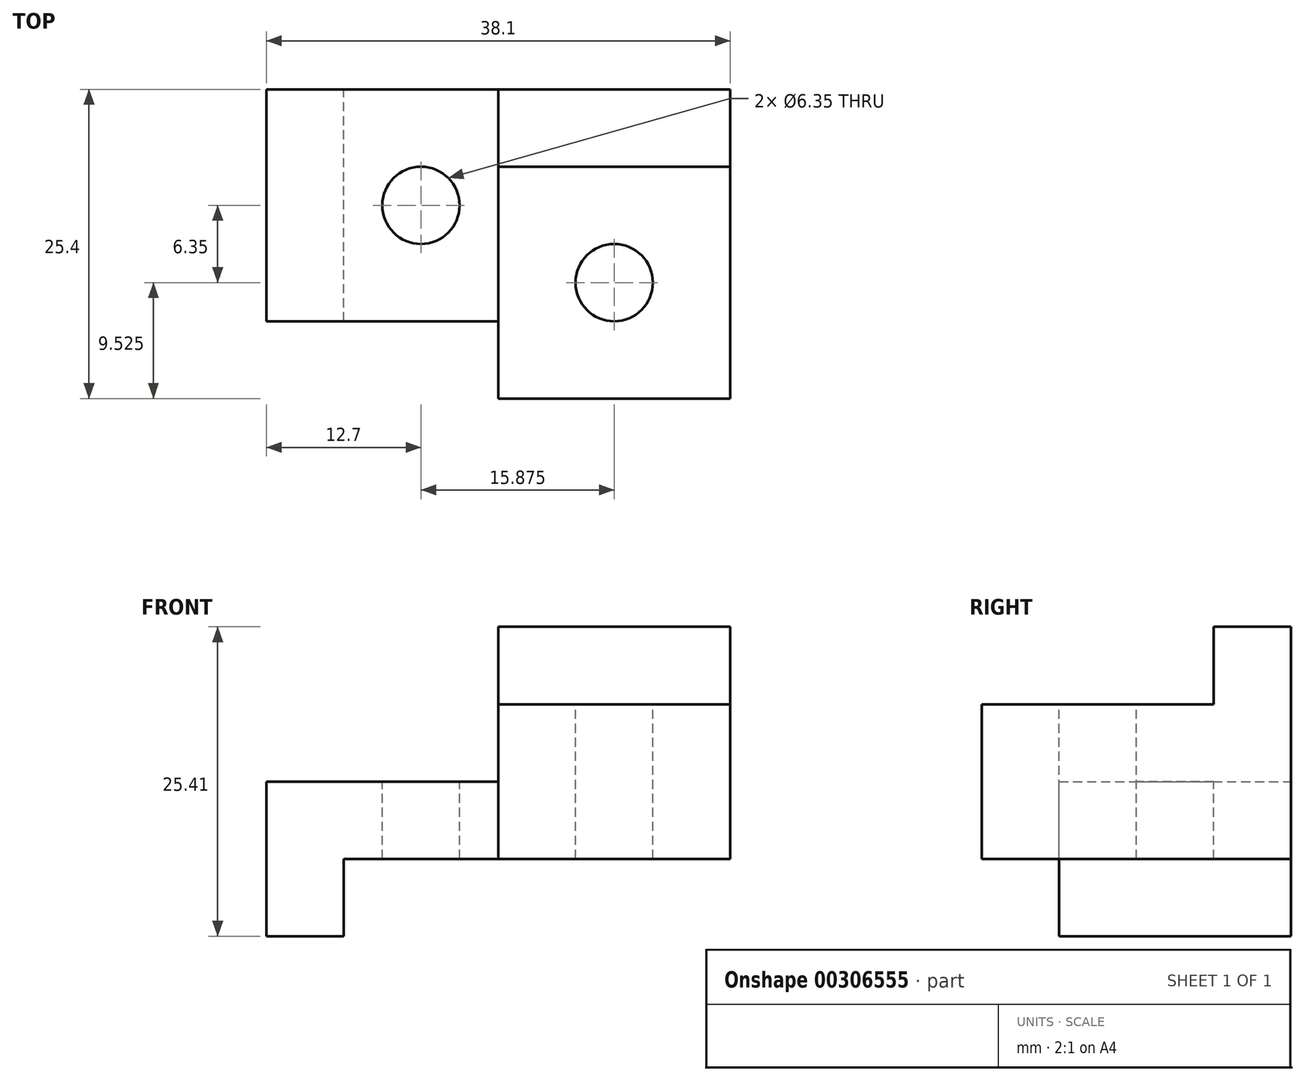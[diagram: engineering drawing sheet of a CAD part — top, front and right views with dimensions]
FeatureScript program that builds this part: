
annotation { "Feature Type Name" : "Feature", "Feature Type Description" : "" }
export const myFeature = defineFeature(function(context is Context, id is Id, definition is map)
    precondition{}
    {
        {
            var Q0;
            Q0=qCreatedBy(makeId("Front.planeOp"),FACE);
            var sketch = newSketch(context, id + "F0", { "sketchPlane" : qUnion([Q0])});
            skLineSegment(sketch, "E0", {"start": v(0, 0) * mm, "end": v(0, 12.7) * mm});
            skLineSegment(sketch, "E1", {"start": v(0, 12.7) * mm, "end": v(19.05, 12.7) * mm});
            skLineSegment(sketch, "E2", {"start": v(19.05, 6.35) * mm, "end": v(6.35, 6.35) * mm});
            skLineSegment(sketch, "E3", {"start": v(6.35, 6.35) * mm, "end": v(6.35, 0) * mm});
            skLineSegment(sketch, "E4", {"start": v(6.35, 0) * mm, "end": v(0, 0) * mm});
            skLineSegment(sketch, "E5", {"start": v(38.1, 25.4) * mm, "end": v(38.1, 6.35) * mm});
            skLineSegment(sketch, "E6", {"start": v(38.1, 6.35) * mm, "end": v(19.05, 6.35) * mm});
            skLineSegment(sketch, "E7", {"start": v(19.05, 6.35) * mm, "end": v(19.05, 12.7) * mm});
            skLineSegment(sketch, "E8", {"start": v(19.05, 12.7) * mm, "end": v(19.05, 25.4) * mm});
            skLineSegment(sketch, "E9", {"start": v(19.05, 25.4) * mm, "end": v(38.1, 25.4) * mm});
            skLineSegment(sketch, "E10", {"start": v(19.05, 19.05) * mm, "end": v(38.1, 19.05) * mm});
            skSolve(sketch);
        }
        {
            var Q0;
            Q0=makeQuery(id+"F0.imprint","IMPRINT",FACE,{"disambiguationData":[TD([[makeQuery(id+"F0.imprint","IMPRINT",EDGE,{"derivedFrom":sQuery(id+"F0.wireOp",EDGE,"E0")}),-1.0]])]});
            extrude(context, id + "F1", {"entities" : qUnion([Q0]), "depth" : 19.05 * mm});
        }
        {
            var Q0;
            {var subQ3=sQuery(id+"F0.wireOp",EDGE,"E6");Q0=makeQuery(id+"F0.imprint","IMPRINT",FACE,{"disambiguationData":[TD([[makeQuery(id+"F0.imprint","IMPRINT",EDGE,{"derivedFrom":subQ3}),-1.0]])]});}
            extrude(context, id + "F2", {"entities" : qUnion([Q0]), "operationType" : NewBodyOperationType.ADD, "depth" : 25.4 * mm});
        }
        {
            var Q0;
            {var subQ0=sQuery(id+"F0.wireOp",EDGE,"E9");Q0=makeQuery(id+"F0.imprint","IMPRINT",FACE,{"disambiguationData":[TD([[makeQuery(id+"F0.imprint","IMPRINT",EDGE,{"derivedFrom":subQ0}),-1.0]])]});}
            extrude(context, id + "F3", {"entities" : qUnion([Q0]), "operationType" : NewBodyOperationType.ADD, "depth" : 6.35 * mm});
        }
        {
            var Q0;
            Q0=makeQuery(id+"F1.opExtrude","SWEPT_FACE",FACE,{"disambiguationData":[OSD([sQuery(id+"F0.wireOp",EDGE,"E1")])]});
            var sketch = newSketch(context, id + "F4", { "sketchPlane" : qUnion([Q0])});
            skLineSegment(sketch, "E11", {"start": v(12.7, 0) * mm, "end": v(12.7, -19.05) * mm, "construction": true});
            skLineSegment(sketch, "E12", {"start": v(0, -9.53) * mm, "end": v(19.05, -9.53) * mm, "construction": true});
            skCircle(sketch, "E13", {"center": v(12.7, -9.53) * mm, "radius": 3.18 * mm});
            skSolve(sketch);
        }
        {
            var Q0;
            Q0=makeQuery(id+"F4.imprint","IMPRINT",FACE,{"disambiguationData":[TD([[makeQuery(id+"F4.imprint","IMPRINT",EDGE,{"derivedFrom":sQuery(id+"F4.wireOp",EDGE,"E13")}),1.0]])]});
            extrude(context, id + "F5", {"entities" : qUnion([Q0]), "operationType" : NewBodyOperationType.REMOVE, "endBound" : BoundingType.THROUGH_ALL, "oppositeDirection" : true, "depth" : 25.4 * mm});
        }
        {
            var Q0;
            Q0=makeQuery(id+"F2.opExtrude","SWEPT_FACE",FACE,{"disambiguationData":[OSD([sQuery(id+"F0.wireOp",EDGE,"E10")])]});
            var sketch = newSketch(context, id + "F6", { "sketchPlane" : qUnion([Q0])});
            skLineSegment(sketch, "E14", {"start": v(28.58, -6.35) * mm, "end": v(28.58, -25.4) * mm, "construction": true});
            skLineSegment(sketch, "E15", {"start": v(19.05, -15.88) * mm, "end": v(38.1, -15.88) * mm, "construction": true});
            skCircle(sketch, "E16", {"center": v(28.58, -15.88) * mm, "radius": 3.18 * mm});
            skSolve(sketch);
        }
        {
            var Q0;
            Q0=makeQuery(id+"F6.imprint","IMPRINT",FACE,{"disambiguationData":[TD([[makeQuery(id+"F6.imprint","IMPRINT",EDGE,{"derivedFrom":sQuery(id+"F6.wireOp",EDGE,"E16")}),1.0]])]});
            extrude(context, id + "F7", {"entities" : qUnion([Q0]), "operationType" : NewBodyOperationType.REMOVE, "endBound" : BoundingType.THROUGH_ALL, "oppositeDirection" : true, "depth" : 25.4 * mm});
        }
    });
